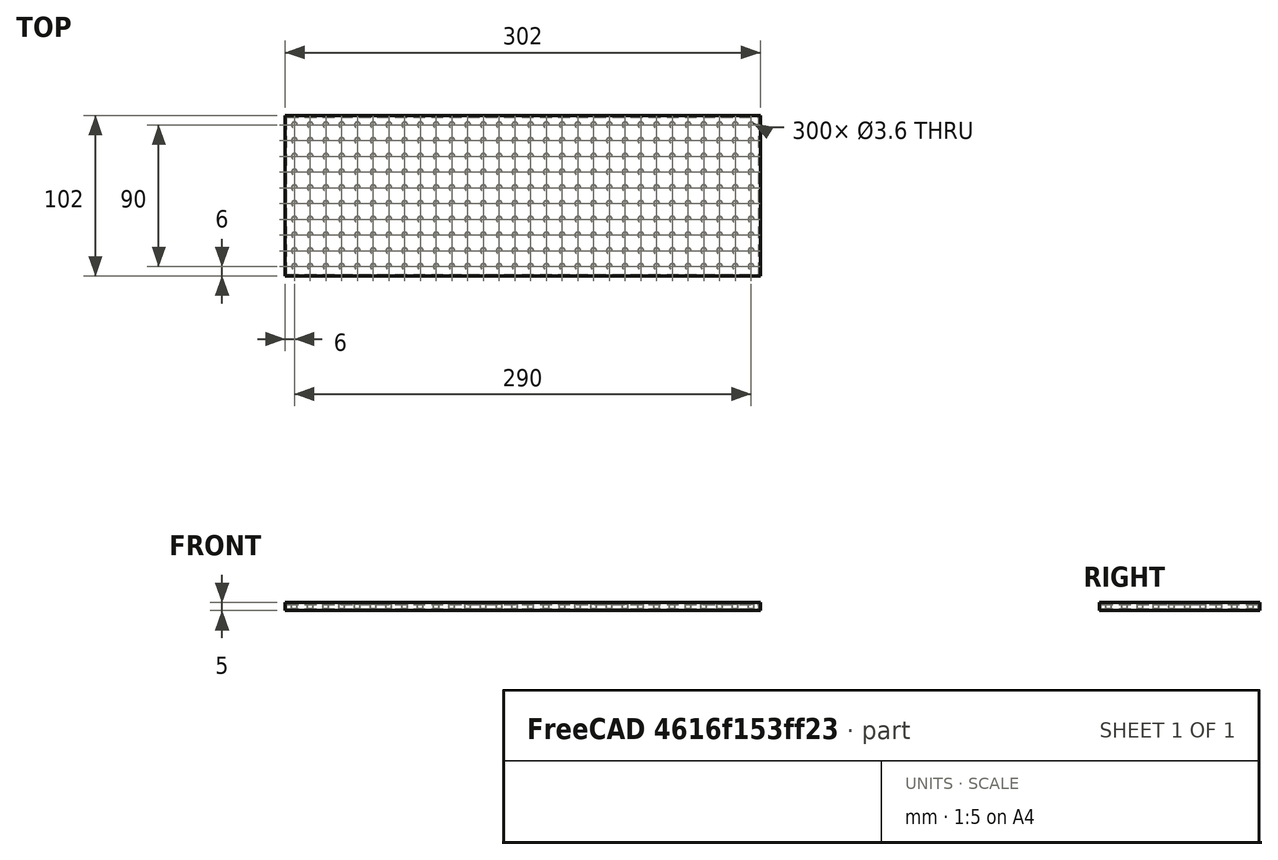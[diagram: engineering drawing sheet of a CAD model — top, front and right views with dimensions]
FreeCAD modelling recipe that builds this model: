
FCSTD DOCUMENT  (FreeCAD 0.19R)
Label: hole_plate2
License: All rights reserved
LicenseURL: http://en.wikipedia.org/wiki/All_rights_reserved
objects: Path::FeaturePython×4, Part::FeaturePython×3, App::DocumentObjectGroup×2, Part::Box×1, Spreadsheet::Sheet×1, Part::Cylinder×1, Part::Cut×1, App::FeaturePython×1, Path::FeatureCompoundPython×1
note: 7 computed .brp shape members not serialized (recipe doc carries the construction recipe); baked Part::Feature solids carry a one-line shape summary decoded from their .brp

FEATURE [Part::Box] Box  label="hole plate cube"
  AttacherType = Attacher::AttachEngine3D
  Height = 3
  Length = 300
  Width = 100
  expr: Width = <<p>>.plate_y
  expr: Length = <<p>>.plate_x
FEATURE [Spreadsheet::Sheet] Spreadsheet  label="p"
  cells = A1=hole_r; B1(hole_r)=1.8; A2=plate_hole_dist; B2(plate_hole_dist)=10; A3=plate_x; B3(plate_x)=300; A4=plate_y; B4(plate_y)=100
FEATURE [Part::Cylinder] Cylinder  label="the hole"
  Angle = 360
  AttacherType = Attacher::AttachEngine3D
  Height = 10
  Radius = 1.8
  expr: Radius = <<p>>.hole_r
FEATURE [Part::FeaturePython] Array  label="hole array"  # Draft array (typed FeaturePython)
  Angle = 360
  ArrayType = 0
  Axis = (0,0,1)
  Base = -> Cylinder
  Center = (0,0,0)
  Fuse = false
  IntervalAxis = (0,0,0)
  IntervalX = (10,0,0)
  IntervalY = (0,10,0)
  IntervalZ = (0,0,1)
  NumberPolar = 1
  NumberX = 30
  NumberY = 10
  NumberZ = 1
  Placement = pos=(5,5,0) rot=(0,0,1;0rad)
  expr: NumberX = floor(<<p>>.plate_x / <<p>>.plate_hole_dist)
  expr: NumberY = floor(<<p>>.plate_y / <<p>>.plate_hole_dist)
  expr: .IntervalX.x = <<p>>.plate_hole_dist
  expr: .Placement.Base.x = <<p>>.plate_hole_dist / 2
  expr: .Placement.Base.y = <<p>>.plate_hole_dist / 2
FEATURE [Part::Cut] Cut  label="hole plate cut"
  Base = -> Box
  Tool = -> Array
FEATURE [App::FeaturePython] SetupSheet  # Path/CAM operation (typed FeaturePython)
  ClearanceHeightExpression = OpStockZMax+SetupSheet.ClearanceHeightOffset
  ClearanceHeightOffset = 0
  CoolantMode = 0
  CoolantModes = None | Flood | Mist
  FinalDepthExpression = OpFinalDepth
  HorizRapid = 100
  SafeHeightExpression = OpStockZMax+SetupSheet.SafeHeightOffset
  SafeHeightOffset = 0
  StartDepthExpression = OpStartDepth
  StepDownExpression = OpToolDiameter
  VertRapid = 100
FEATURE [Part::FeaturePython] Clone  label="Model-hole plate cut"  # Draft clone (typed FeaturePython)
  AttacherType = Attacher::AttachEngine3D
  Fuse = false
  Objects = -> [Cut]
  PathResource = Model
  Scale = (1,1,1)
FEATURE [App::DocumentObjectGroup] Model
  Group = -> [Clone]
FEATURE [Path::FeaturePython] T3__laser  label="T3: laser"  # Path/CAM operation (typed FeaturePython)
  HorizFeed = 0.5
  HorizRapid = 100
  SpindleDir = 0
  SpindleSpeed = 1000
  ToolNumber = 3
  VertFeed = 0.5
  VertRapid = 100
  expr: HorizRapid = SetupSheet.HorizRapid
  expr: VertRapid = SetupSheet.VertRapid
FEATURE [Part::FeaturePython] Stock  # WARN: FeaturePython — macro-defined, semantics opaque (R4)
  Base = -> Model
  ExtXneg = 1
  ExtXpos = 1
  ExtYneg = 1
  ExtYpos = 1
  ExtZneg = 1
  ExtZpos = 1
  StockType = FromBase
FEATURE [Path::FeaturePython] Contour  # Path/CAM operation (typed FeaturePython)
  Active = true
  AreaParams:
    Tolerance = 1e-07
    FitArcs = True
    Simplify = False
    CleanDistance = 0.0
    Accuracy = 0.01
    Unit = 1.0
    MinArcPoints = 4
    MaxArcPoints = 100
    ClipperScale = 10000000.0
    Fill = 0
    Coplanar = 2
    Reorient = True
    Outline = False
    Explode = False
    OpenMode = 0
    Deflection = 0.01
    SubjectFill = 0
    ClipFill = 0
    Offset = 0.1
    ExtraPass = 0
    Stepover = 0.0
    LastStepover = 0.0
    JoinType = 0
    EndType = 0
    MiterLimit = 2.0
    RoundPrecision = 0.0
    PocketMode = 0
    ToolRadius = 1.0
    PocketExtraOffset = 0.0
    PocketStepover = 0.0
    PocketLastStepover = 0.0
    FromCenter = False
    Angle = 45.0
    AngleShift = 0.0
    Shift = 0.0
    Thicken = False
    SectionCount = -1
    Stepdown = 1.0
    SectionOffset = 0.0
    SectionTolerance = 1e-06
    SectionMode = 2
    Project = False
  ClearanceHeight = 1
  Direction = 0
  FinalDepth = 0
  JoinType = 0
  MiterLimit = 0.1
  OffsetExtra = 0
  OpFinalDepth = -1
  OpStartDepth = 4
  OpStockZMax = 4
  OpStockZMin = -1
  OpToolDiameter = 0.2
  PathParams = {'orientation': 1, 'feedrate': 0.5, 'feedrate_v': 0.5, 'verbose': True, 'resume_height': 1.0, 'retraction': 1.0, 'return_end': True, 'preamble': False}
  SafeHeight = 1
  Side = 0
  StartDepth = 0.1
  StartPoint = (0,0,0)
  StepDown = 0.2
  ToolController = -> T3__laser
  UseComp = true
  UseStartPoint = false
FEATURE [Path::FeaturePython] Engrave  # Path/CAM operation (typed FeaturePython)
  Active = true
  Base = -> [Clone]
  ClearanceHeight = 1
  FinalDepth = 0
  OpFinalDepth = 2.8
  OpStartDepth = 3
  OpStockZMax = 4
  OpStockZMin = -1
  OpToolDiameter = 0.2
  SafeHeight = 1
  StartDepth = 4.1
  StartVertex = 0
  StepDown = 0.2
  ToolController = -> T3__laser
  expr: StepDown = OpToolDiameter
FEATURE [Path::FeatureCompoundPython] Operations  # Path/CAM operation (typed FeaturePython)
  Group = -> [Contour,Engrave]
  UsePlacements = false
FEATURE [App::DocumentObjectGroup] Tools
  Group = -> [T3__laser]
FEATURE [Path::FeaturePython] Job  label="hole plate job"  # Path/CAM operation (typed FeaturePython)
  GeometryTolerance = 0.01
  Model = -> Model
  Operations = -> Operations
  PostProcessor = 1
  PostProcessorOutputFile = <userpath>/work/roborep/freecad/hole_plate/hole_plate.gcode
  SetupSheet = -> SetupSheet
  Stock = -> Stock
  Tools = -> Tools
